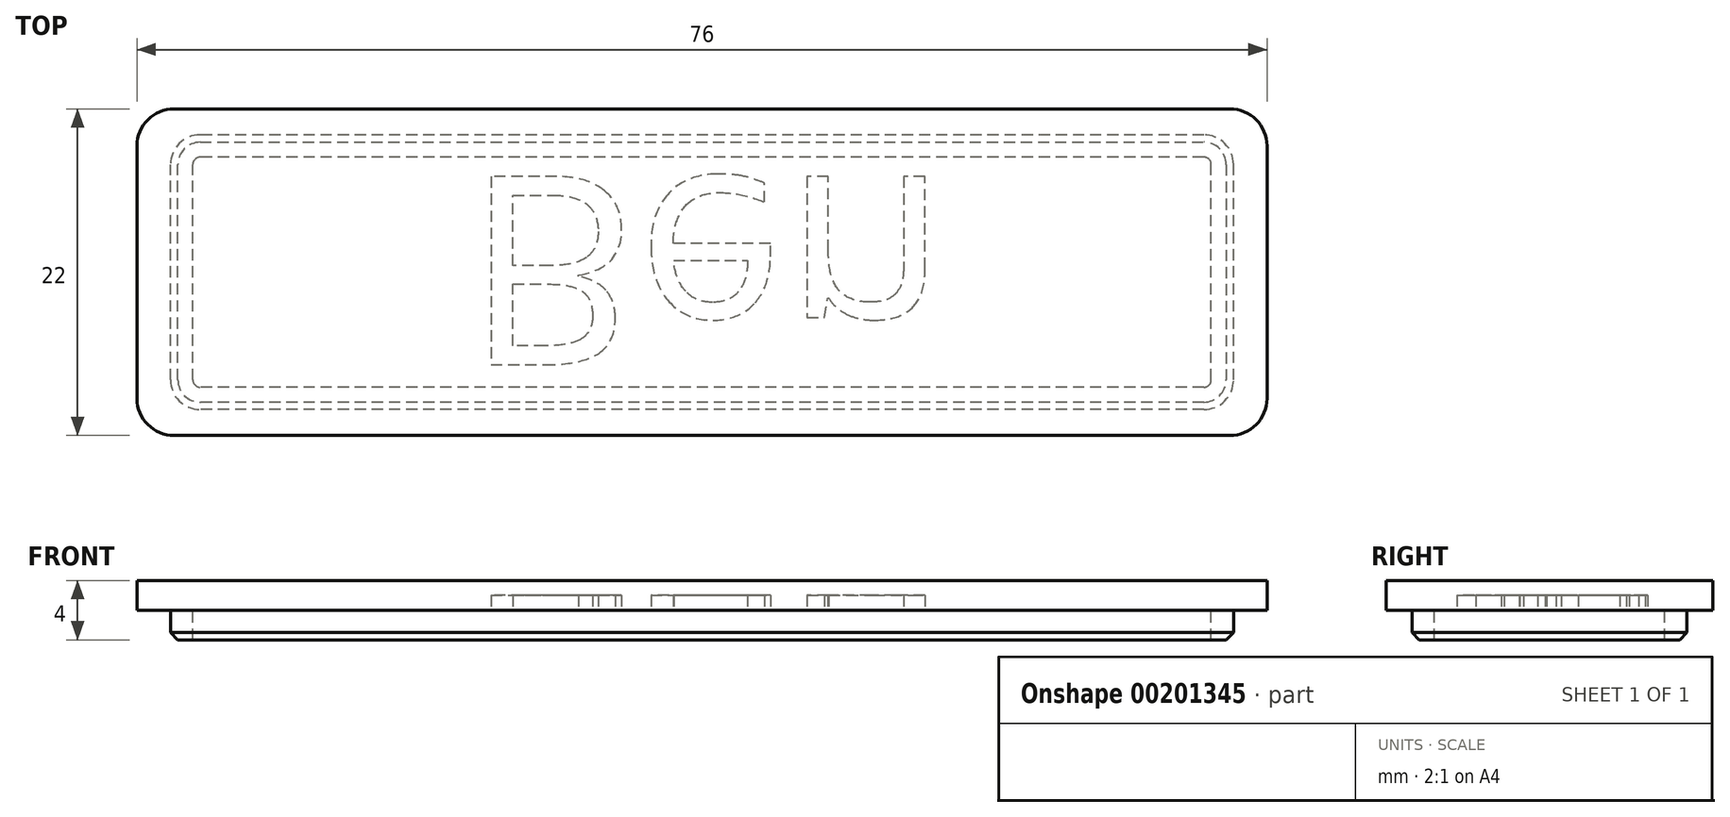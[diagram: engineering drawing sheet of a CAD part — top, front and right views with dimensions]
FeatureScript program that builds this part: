
annotation { "Feature Type Name" : "Feature", "Feature Type Description" : "" }
export const myFeature = defineFeature(function(context is Context, id is Id, definition is map)
    precondition{}
    {
        {
            var Q0;
            Q0=qCreatedBy(makeId("Top.planeOp"),FACE);
            var sketch = newSketch(context, id + "F0", { "sketchPlane" : qUnion([Q0])});
            skLineSegment(sketch, "E0.bottom", {"start": v(35.5, -11) * mm, "end": v(-35.5, -11) * mm});
            skLineSegment(sketch, "E0.top", {"start": v(35.5, 11) * mm, "end": v(-35.5, 11) * mm});
            skLineSegment(sketch, "E0.left", {"start": v(38, -8.5) * mm, "end": v(38, 8.5) * mm});
            skLineSegment(sketch, "E0.right", {"start": v(-38, -8.5) * mm, "end": v(-38, 8.5) * mm});
            skPoint(sketch, "E0.middle", {"position": v(0, 0) * mm});
            skArc(sketch, "E1.filletArc", {"start": v(-35.5, 11) * mm, "mid": v(-37.27, 10.27) * mm, "end": v(-38, 8.5) * mm});
            skPoint(sketch, "E2.visualSharp", {"position": v(38, 11) * mm});
            skArc(sketch, "E2.filletArc", {"start": v(38, 8.5) * mm, "mid": v(37.27, 10.27) * mm, "end": v(35.5, 11) * mm});
            skPoint(sketch, "E3.visualSharp", {"position": v(38, -11) * mm});
            skArc(sketch, "E3.filletArc", {"start": v(35.5, -11) * mm, "mid": v(37.27, -10.27) * mm, "end": v(38, -8.5) * mm});
            skPoint(sketch, "E4.visualSharp", {"position": v(-38, -11) * mm});
            skArc(sketch, "E4.filletArc", {"start": v(-38, -8.5) * mm, "mid": v(-37.27, -10.27) * mm, "end": v(-35.5, -11) * mm});
            skLineSegment(sketch, "E5.bottom", {"start": v(33.75, -9.25) * mm, "end": v(-33.75, -9.25) * mm});
            skLineSegment(sketch, "E5.top", {"start": v(33.75, 9.25) * mm, "end": v(-33.75, 9.25) * mm});
            skLineSegment(sketch, "E5.left", {"start": v(35.75, -7.25) * mm, "end": v(35.75, 7.25) * mm});
            skLineSegment(sketch, "E5.right", {"start": v(-35.75, -7.25) * mm, "end": v(-35.75, 7.25) * mm});
            skPoint(sketch, "E6.visualSharp", {"position": v(-35.75, 9.25) * mm});
            skArc(sketch, "E6.filletArc", {"start": v(-33.75, 9.25) * mm, "mid": v(-35.16, 8.66) * mm, "end": v(-35.75, 7.25) * mm});
            skPoint(sketch, "E7.visualSharp", {"position": v(35.75, 9.25) * mm});
            skArc(sketch, "E7.filletArc", {"start": v(35.75, 7.25) * mm, "mid": v(35.16, 8.66) * mm, "end": v(33.75, 9.25) * mm});
            skPoint(sketch, "E8.visualSharp", {"position": v(35.75, -9.25) * mm});
            skArc(sketch, "E8.filletArc", {"start": v(33.75, -9.25) * mm, "mid": v(35.16, -8.66) * mm, "end": v(35.75, -7.25) * mm});
            skPoint(sketch, "E9.visualSharp", {"position": v(-35.75, -9.25) * mm});
            skArc(sketch, "E9.filletArc", {"start": v(-35.75, -7.25) * mm, "mid": v(-35.16, -8.66) * mm, "end": v(-33.75, -9.25) * mm});
            skArc(sketch, "E10.0", {"start": v(34.25, 7.25) * mm, "mid": v(34.1, 7.6) * mm, "end": v(33.75, 7.75) * mm});
            skLineSegment(sketch, "E10.1", {"start": v(34.25, -7.25) * mm, "end": v(34.25, 7.25) * mm});
            skLineSegment(sketch, "E10.2", {"start": v(33.75, 7.75) * mm, "end": v(-33.75, 7.75) * mm});
            skArc(sketch, "E10.3", {"start": v(33.75, -7.75) * mm, "mid": v(34.1, -7.6) * mm, "end": v(34.25, -7.25) * mm});
            skArc(sketch, "E10.4", {"start": v(-33.75, 7.75) * mm, "mid": v(-34.1, 7.6) * mm, "end": v(-34.25, 7.25) * mm});
            skLineSegment(sketch, "E10.5", {"start": v(-34.25, -7.25) * mm, "end": v(-34.25, 7.25) * mm});
            skArc(sketch, "E10.6", {"start": v(-34.25, -7.25) * mm, "mid": v(-34.1, -7.6) * mm, "end": v(-33.75, -7.75) * mm});
            skLineSegment(sketch, "E10.7", {"start": v(33.75, -7.75) * mm, "end": v(-33.75, -7.75) * mm});
            skSolve(sketch);
        }
        {
            var Q0;
            Q0 = qSketchRegion(id + "F0", true);
            var Q1;
            Q1=makeQuery(id+"F0.imprint","IMPRINT",FACE,{"disambiguationData":[TD([[makeQuery(id+"F0.imprint","IMPRINT",EDGE,{"derivedFrom":sQuery(id+"F0.wireOp",EDGE,"E5.bottom")}),-1.0]])]});
            var Q2;
            Q2=makeQuery(id+"F0.imprint","IMPRINT",FACE,{"disambiguationData":[TD([[makeQuery(id+"F0.imprint","IMPRINT",EDGE,{"derivedFrom":sQuery(id+"F0.wireOp",EDGE,"E10.0")}),1.0]])]});
            extrude(context, id + "F1", {"entities" : qUnion([Q0, Q1, Q2]), "depth" : 2 * mm});
        }
        {
            var Q0;
            Q0=makeQuery(id+"F0.imprint","IMPRINT",FACE,{"disambiguationData":[TD([[makeQuery(id+"F0.imprint","IMPRINT",EDGE,{"derivedFrom":sQuery(id+"F0.wireOp",EDGE,"E5.bottom")}),-1.0]])]});
            extrude(context, id + "F2", {"entities" : qUnion([Q0]), "operationType" : NewBodyOperationType.ADD, "oppositeDirection" : true, "depth" : 2 * mm});
        }
        {
            var Q0;
            Q0=makeQuery(id+"F2.opExtrude","CAP_EDGE",EDGE,{"disambiguationData":[OSD([sQuery(id+"F0.wireOp",EDGE,"E5.top")])],"isStart":false});
            chamfer(context, id + "F3", {"entities" : qUnion([Q0]), "width" : 0.5 * mm, "tangentPropagation" : true});
        }
        {
            var Q0;
            Q0=makeQuery(id+"F2.boolean.opBoolean","SPLIT",FACE,{"disambiguationData":[TD([makeQuery(id+"F2.opExtrude","SWEPT_FACE",FACE,{"disambiguationData":[OSD([sQuery(id+"F0.wireOp",EDGE,"E10.0")])]})])],"derivedFrom":makeQuery(id+"F1.opExtrude","CAP_FACE",FACE,{"disambiguationData":[OSD([sQuery(id+"F0.wireOp",EDGE,"E0.bottom"),sQuery(id+"F0.wireOp",EDGE,"E0.top"),sQuery(id+"F0.wireOp",EDGE,"E0.left"),sQuery(id+"F0.wireOp",EDGE,"E0.right"),sQuery(id+"F0.wireOp",EDGE,"E1.filletArc"),sQuery(id+"F0.wireOp",EDGE,"E2.filletArc"),sQuery(id+"F0.wireOp",EDGE,"E3.filletArc"),sQuery(id+"F0.wireOp",EDGE,"E4.filletArc")])],"isStart":true})});
            var sketch = newSketch(context, id + "F4", { "sketchPlane" : qUnion([Q0])});
            skText(sketch, "E11", { "text": "Ben", "fontName": "OpenSans-Regular.ttf"});
            const initialGuessF4  = {"E11": [-0.01593, -0.00644, 1, 0, 0.01278]};
            skSetInitialGuess(sketch, initialGuessF4);
            skSolve(sketch);
        }
        {
            var Q0;
            Q0 = qSketchRegion(id + "F4", true);
            extrude(context, id + "F5", {"entities" : qUnion([Q0]), "operationType" : NewBodyOperationType.REMOVE, "oppositeDirection" : true, "depth" : 1 * mm});
        }
    });
